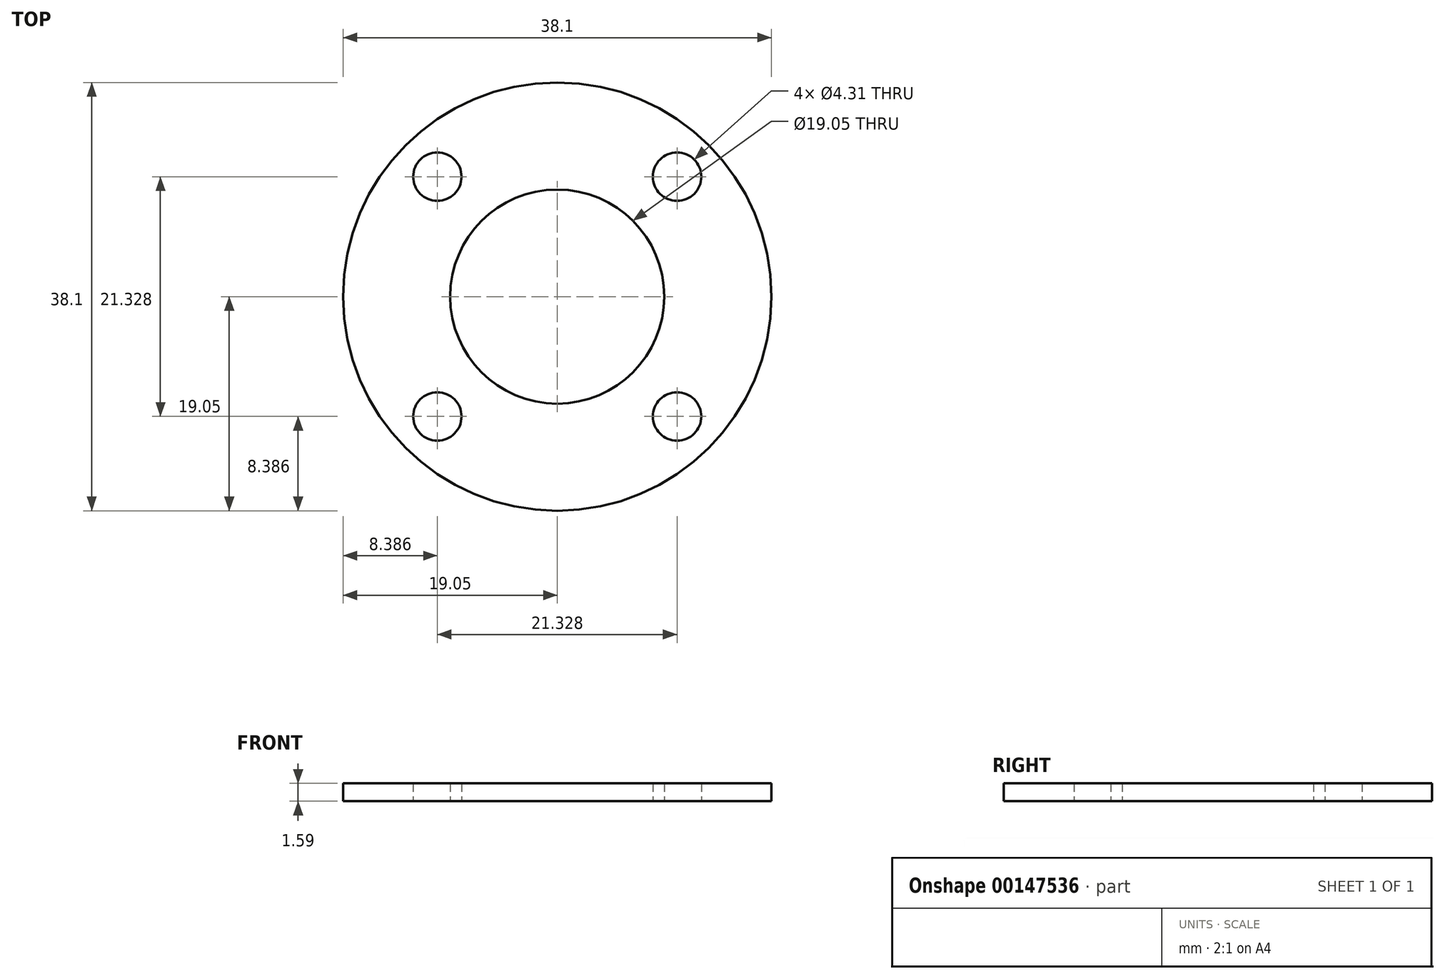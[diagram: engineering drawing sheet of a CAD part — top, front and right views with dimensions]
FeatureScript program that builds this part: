
annotation { "Feature Type Name" : "Feature", "Feature Type Description" : "" }
export const myFeature = defineFeature(function(context is Context, id is Id, definition is map)
    precondition{}
    {
        {
            var Q0;
            Q0=qCreatedBy(makeId("Top.planeOp"),FACE);
            var sketch = newSketch(context, id + "F0", { "sketchPlane" : qUnion([Q0])});
            skCircle(sketch, "E0", {"center": v(0, 0) * mm, "radius": 19.05 * mm});
            skCircle(sketch, "E1", {"center": v(0, 0) * mm, "radius": 9.53 * mm});
            skLineSegment(sketch, "E2.bottom", {"start": v(10.66, -10.66) * mm, "end": v(-10.66, -10.66) * mm, "construction": true});
            skLineSegment(sketch, "E2.top", {"start": v(10.66, 10.66) * mm, "end": v(-10.66, 10.66) * mm, "construction": true});
            skLineSegment(sketch, "E2.left", {"start": v(10.66, -10.66) * mm, "end": v(10.66, 10.66) * mm, "construction": true});
            skLineSegment(sketch, "E2.right", {"start": v(-10.66, -10.66) * mm, "end": v(-10.66, 10.66) * mm, "construction": true});
            skCircle(sketch, "E3", {"center": v(10.66, -10.66) * mm, "radius": 3.97 * mm, "construction": true});
            skCircle(sketch, "E4", {"center": v(10.66, 10.66) * mm, "radius": 2.15 * mm});
            skCircle(sketch, "E5", {"center": v(-10.66, -10.66) * mm, "radius": 2.15 * mm});
            skCircle(sketch, "E6", {"center": v(10.66, -10.66) * mm, "radius": 2.15 * mm});
            skCircle(sketch, "E7", {"center": v(-10.66, 10.66) * mm, "radius": 2.15 * mm});
            skCircle(sketch, "E8", {"center": v(0, 0) * mm, "radius": 11.11 * mm, "construction": true});
            skSolve(sketch);
        }
        {
            var Q0;
            Q0=qSketchRegion(id+"F0",true);
            extrude(context, id + "F1", {"entities" : qUnion([Q0]), "depth" : 1.59 * mm});
        }
    });
